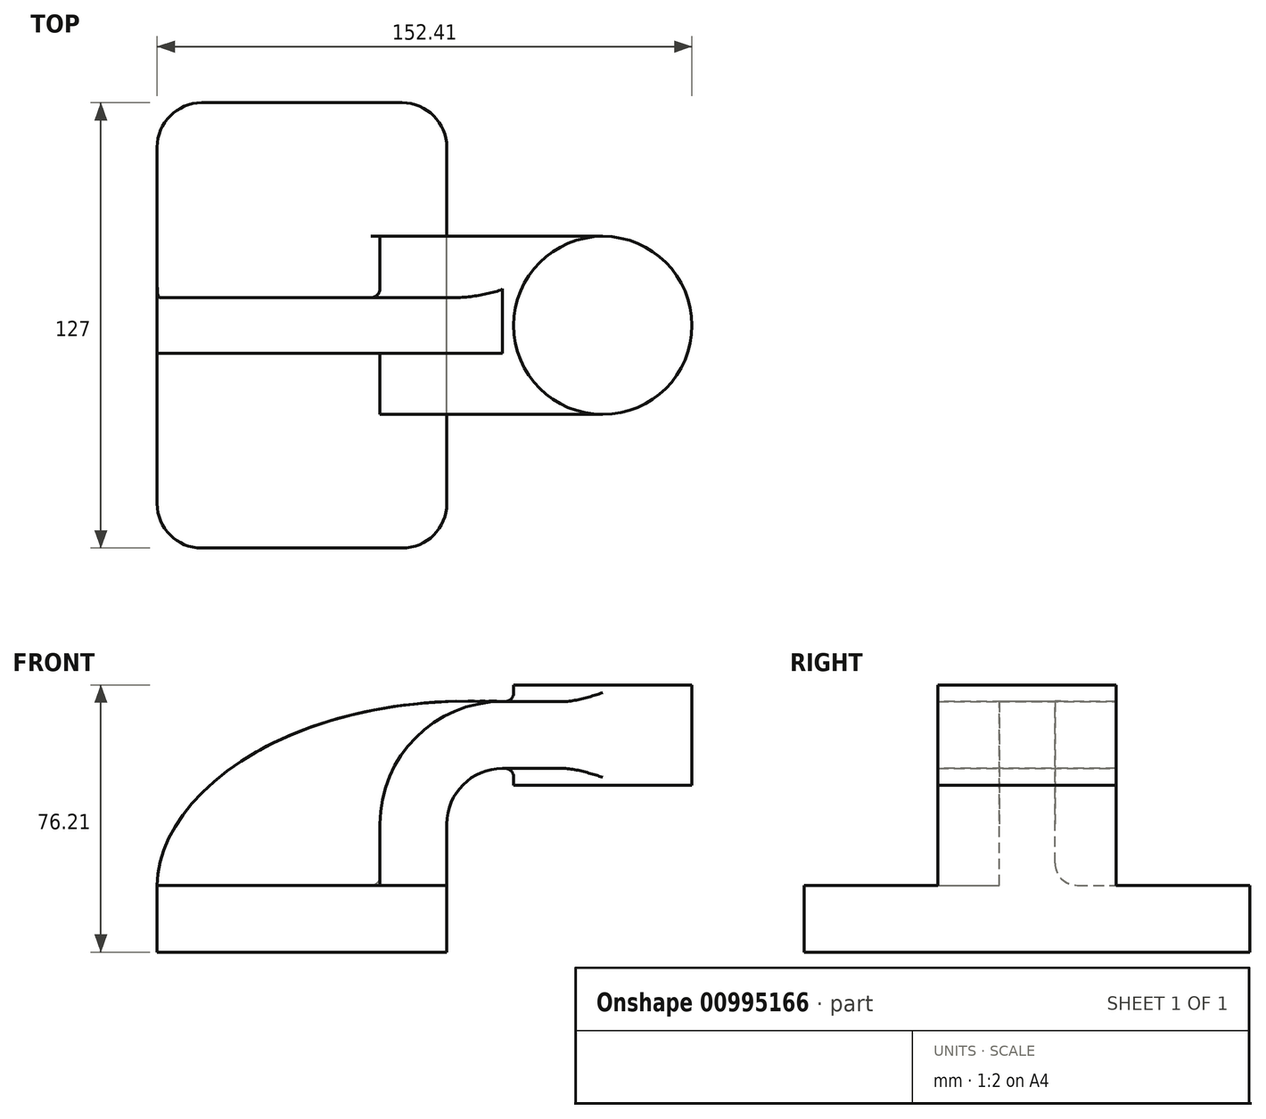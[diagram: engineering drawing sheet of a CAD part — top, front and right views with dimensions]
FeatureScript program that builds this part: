
annotation { "Feature Type Name" : "Feature", "Feature Type Description" : "" }
export const myFeature = defineFeature(function(context is Context, id is Id, definition is map)
    precondition{}
    {
        {
            var Q0;
            Q0=qCreatedBy(makeId("Front.planeOp"),FACE);
            var sketch = newSketch(context, id + "F0", { "sketchPlane" : qUnion([Q0])});
            skLineSegment(sketch, "E0.bottom", {"start": v(-41.27, -9.52) * mm, "end": v(41.28, -9.52) * mm});
            skLineSegment(sketch, "E0.top", {"start": v(-41.28, 9.53) * mm, "end": v(41.27, 9.53) * mm});
            skLineSegment(sketch, "E0.left", {"start": v(-41.27, -9.52) * mm, "end": v(-41.28, 9.53) * mm});
            skLineSegment(sketch, "E0.right", {"start": v(41.28, -9.52) * mm, "end": v(41.28, 9.53) * mm});
            skPoint(sketch, "E0.middle", {"position": v(0, 0) * mm});
            skLineSegment(sketch, "E1.bottom", {"start": v(60.33, 38.1) * mm, "end": v(111.13, 38.1) * mm});
            skLineSegment(sketch, "E1.top", {"start": v(60.33, 66.68) * mm, "end": v(111.13, 66.68) * mm});
            skLineSegment(sketch, "E1.left", {"start": v(60.33, 38.1) * mm, "end": v(60.33, 66.68) * mm});
            skLineSegment(sketch, "E1.right", {"start": v(111.13, 38.1) * mm, "end": v(111.13, 66.68) * mm});
            skPoint(sketch, "E1.middle", {"position": v(85.73, 52.39) * mm});
            skLineSegment(sketch, "E2", {"start": v(41.27, 9.53) * mm, "end": v(41.27, 26.99) * mm});
            skArc(sketch, "E3", {"start": v(41.27, 26.99) * mm, "mid": v(45.92, 38.21) * mm, "end": v(57.15, 42.86) * mm});
            skLineSegment(sketch, "E4", {"start": v(57.15, 42.86) * mm, "end": v(85.73, 42.86) * mm});
            skLineSegment(sketch, "E5.0", {"start": v(57.15, 61.91) * mm, "end": v(85.73, 61.91) * mm});
            skArc(sketch, "E5.1", {"start": v(22.23, 26.99) * mm, "mid": v(32.45, 51.68) * mm, "end": v(57.15, 61.91) * mm});
            skLineSegment(sketch, "E5.2", {"start": v(22.22, 9.53) * mm, "end": v(22.22, 26.99) * mm});
            skLineSegment(sketch, "E6", {"start": v(85.73, 38.1) * mm, "end": v(85.73, 66.68) * mm});
            skFitSpline(sketch, "E7", {"points": [v(-41.28, 9.53) * mm, v(57.15, 61.91) * mm], "startDerivative": vector(0.2, 75.54) * mm, "endDerivative": vector(185.2, -8.8) * mm});
            skSolve(sketch);
        }
        {
            var Q0;
            Q0=makeQuery(id+"F0.imprint","IMPRINT",FACE,{"disambiguationData":[TD([[makeQuery(id+"F0.imprint","IMPRINT",EDGE,{"derivedFrom":sQuery(id+"F0.wireOp",EDGE,"E0.bottom")}),1.0]])]});
            extrude(context, id + "F1", {"entities" : qUnion([Q0]), "endBound" : BoundingType.SYMMETRIC, "depth" : 127 * mm, "offsetDistance" : 25.4 * mm});
        }
        {
            var Q0;
            {var subQ1=sQuery(id+"F0.wireOp",EDGE,"E2");Q0=makeQuery(id+"F0.imprint","IMPRINT",FACE,{"disambiguationData":[TD([[makeQuery(id+"F0.imprint","IMPRINT",EDGE,{"derivedFrom":subQ1}),1.0]])]});}
            var Q1;
            {var subQ0=sQuery(id+"F0.wireOp",EDGE,"E4");var subQ1=sQuery(id+"F0.wireOp",EDGE,"E1.left");var subQ2=makeQuery(id+"F0.imprint","INTERSECT",VERTEX,{"derivedFrom":[subQ1,subQ0]});Q1=makeQuery(id+"F0.imprint","IMPRINT",FACE,{"disambiguationData":[TD([[makeQuery(id+"F0.imprint","IMPRINT",EDGE,{"disambiguationData":[TD([[subQ2,-1.0]])],"derivedFrom":subQ1}),-1.0]])]});}
            extrude(context, id + "F2", {"entities" : qUnion([Q0, Q1]), "operationType" : NewBodyOperationType.ADD, "endBound" : BoundingType.SYMMETRIC, "depth" : 50.8 * mm, "offsetDistance" : 25.4 * mm});
        }
        {
            var Q0;
            {var subQ3=sQuery(id+"F0.wireOp",EDGE,"E5.2");Q0=makeQuery(id+"F0.imprint","IMPRINT",FACE,{"disambiguationData":[TD([[makeQuery(id+"F0.imprint","IMPRINT",EDGE,{"derivedFrom":subQ3}),1.0]])]});}
            extrude(context, id + "F3", {"entities" : qUnion([Q0]), "operationType" : NewBodyOperationType.ADD, "endBound" : BoundingType.SYMMETRIC, "depth" : 15.88 * mm, "offsetDistance" : 25.4 * mm});
        }
        {
            var Q0;
            {var subQ4=sQuery(id+"F0.wireOp",EDGE,"E1.right");Q0=makeQuery(id+"F0.imprint","IMPRINT",FACE,{"disambiguationData":[TD([[makeQuery(id+"F0.imprint","IMPRINT",EDGE,{"derivedFrom":subQ4}),1.0]])]});}
            var Q1;
            Q1=sQuery(id+"F0.wireOp",EDGE,"E6");
            revolve(context, id + "F4", {"operationType" : NewBodyOperationType.ADD, "surfaceOperationType" : NewSurfaceOperationType.NEW, "entities" : qUnion([Q0]), "axis" : qUnion([Q1]), "revolveType" : RevolveType.FULL});
        }
        {
            var Q0;
            Q0=makeQuery(id+"F1.opExtrude","CAP_EDGE",EDGE,{"disambiguationData":[OSD([sQuery(id+"F0.wireOp",EDGE,"E0.left")])],"isStart":false});
            var Q1;
            Q1=makeQuery(id+"F1.opExtrude","CAP_EDGE",EDGE,{"disambiguationData":[OSD([sQuery(id+"F0.wireOp",EDGE,"E0.right")])],"isStart":false});
            var Q2;
            Q2=makeQuery(id+"F1.opExtrude","CAP_EDGE",EDGE,{"disambiguationData":[OSD([sQuery(id+"F0.wireOp",EDGE,"E0.right")])],"isStart":true});
            var Q3;
            Q3=makeQuery(id+"F1.opExtrude","CAP_EDGE",EDGE,{"disambiguationData":[OSD([sQuery(id+"F0.wireOp",EDGE,"E0.left")])],"isStart":true});
            fillet(context, id + "F5", {"entities" : qUnion([Q0, Q1, Q2, Q3]), "radius" : 12.7 * mm, "tangentPropagation" : true, "allowEdgeOverflow" : false});
        }
        {
            var Q0;
            Q0=makeQuery(id+"F2.opExtrude","CAP_EDGE",EDGE,{"disambiguationData":[OSD([sQuery(id+"F0.wireOp",EDGE,"E0.top")])],"isStart":false});
            var Q1;
            Q1=makeQuery(id+"F3.opExtrude","CAP_EDGE",EDGE,{"disambiguationData":[OSD([sQuery(id+"F0.wireOp",EDGE,"E0.top")])],"isStart":false});
            var Q2;
            Q2=makeQuery(id+"F2.opExtrude","CAP_EDGE",EDGE,{"disambiguationData":[OSD([sQuery(id+"F0.wireOp",EDGE,"E0.top")])],"isStart":true});
            var Q3;
            Q3=makeQuery(id+"F3.opExtrude","CAP_EDGE",EDGE,{"disambiguationData":[OSD([sQuery(id+"F0.wireOp",EDGE,"E0.top")])],"isStart":true});
            fillet(context, id + "F6", {"entities" : qUnion([Q0, Q1, Q2, Q3]), "radius" : 6.35 * mm, "tangentPropagation" : true, "allowEdgeOverflow" : false});
        }
        {
            var Q0;
            Q0=makeQuery(id+"F3.opExtrude","CAP_EDGE",EDGE,{"disambiguationData":[OSD([sQuery(id+"F0.wireOp",EDGE,"E5.2")])],"isStart":true});
            var Q1;
            Q1=makeQuery(id+"F3.opExtrude","CAP_EDGE",EDGE,{"disambiguationData":[OSD([sQuery(id+"F0.wireOp",EDGE,"E5.2")])],"isStart":false});
            var Q2;
            Q2=makeQuery(id+"F4.boolean.opBoolean","INTERSECT",EDGE,{"derivedFrom":[makeQuery(id+"F2.opExtrude","SWEPT_FACE",FACE,{"disambiguationData":[OSD([sQuery(id+"F0.wireOp",EDGE,"E5.0")])]}),makeQuery(id+"F4.opRevolve","SWEPT_FACE",FACE,{"disambiguationData":[OSD([sQuery(id+"F0.wireOp",EDGE,"E1.right")])]})]});
            var Q3;
            Q3=makeQuery(id+"F4.boolean.opBoolean","INTERSECT",EDGE,{"derivedFrom":[makeQuery(id+"F2.opExtrude","SWEPT_FACE",FACE,{"disambiguationData":[OSD([sQuery(id+"F0.wireOp",EDGE,"E4")])]}),makeQuery(id+"F4.opRevolve","SWEPT_FACE",FACE,{"disambiguationData":[OSD([sQuery(id+"F0.wireOp",EDGE,"E1.right")])]})]});
            fillet(context, id + "F7", {"entities" : qUnion([Q0, Q1, Q2, Q3]), "radius" : 2.54 * mm, "tangentPropagation" : true, "allowEdgeOverflow" : false});
        }
    });
